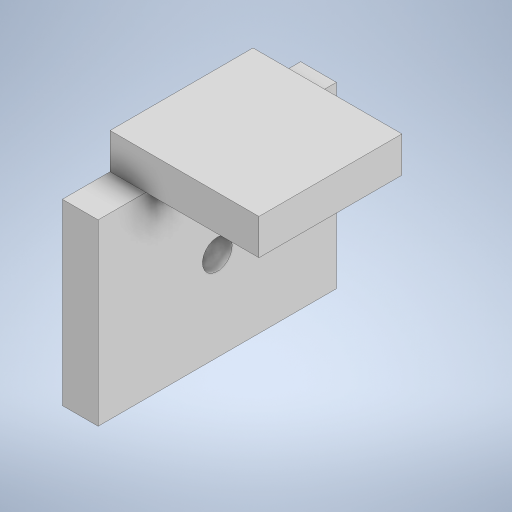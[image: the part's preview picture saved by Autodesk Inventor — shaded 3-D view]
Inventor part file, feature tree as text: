
AUTODESK INVENTOR PART (.ipt)
format: ipt  version: 2024 (Build 280153000, 153)  size: 221,696 bytes
history: native  units: mm
features: extrude x2, other x1, sketch x1
ambient origin geometry x8: Origin, YZ Plane, XZ Plane, XY Plane, X Axis, Y Axis, Z Axis, Center Point
bodies: Body1 (feature_tree)
feature tree (4):
  other  "솔리드1"
  sketch  "스케치1"
  extrude  "돌출1"  Depth=15.0mm
  extrude  "돌출2"  Depth=20.0mm
